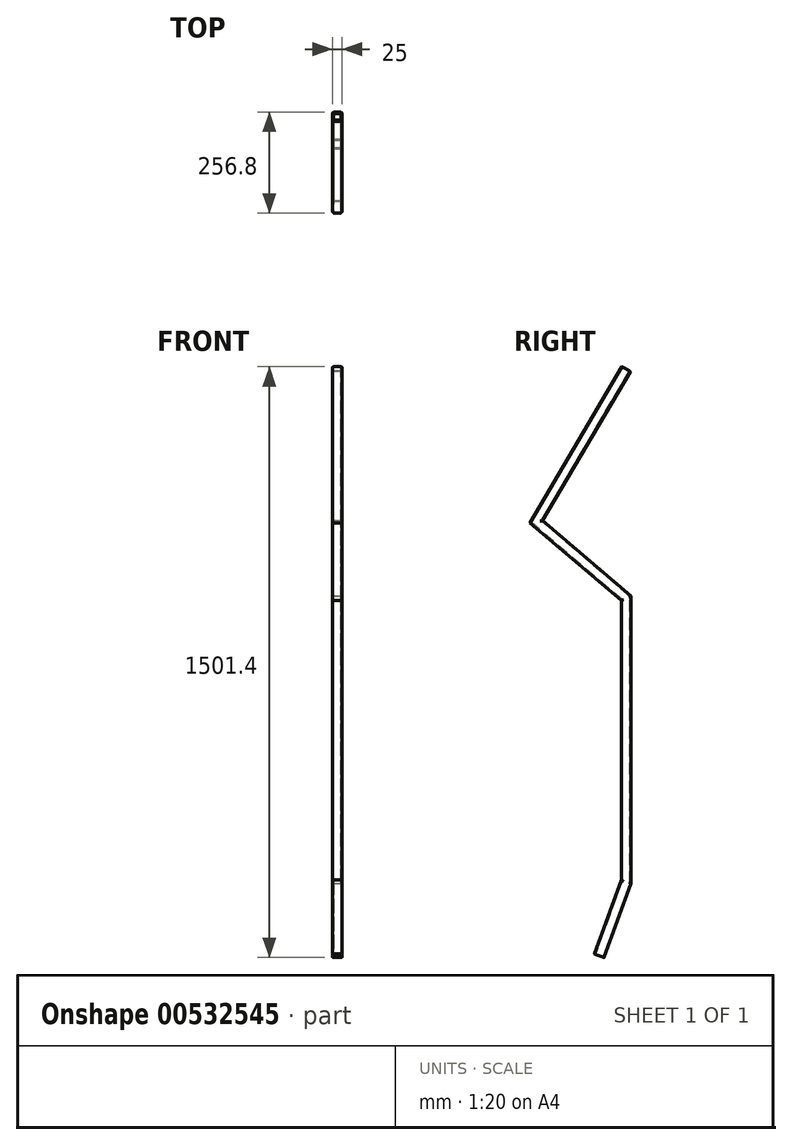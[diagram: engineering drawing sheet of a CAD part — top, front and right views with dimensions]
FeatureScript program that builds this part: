
annotation { "Feature Type Name" : "Feature", "Feature Type Description" : "" }
export const myFeature = defineFeature(function(context is Context, id is Id, definition is map)
    precondition{}
    {
        {
            var Q0;
            Q0=qCreatedBy(makeId("Right.planeOp"),FACE);
            var sketch = newSketch(context, id + "F0", { "sketchPlane" : qUnion([Q0])});
            skLineSegment(sketch, "E0", {"start": v(0, 1302.57) * mm, "end": v(-228.21, 914.73) * mm});
            skLineSegment(sketch, "E1", {"start": v(-228.21, 914.73) * mm, "end": v(0, 720) * mm});
            skLineSegment(sketch, "E2", {"start": v(0, 720) * mm, "end": v(0, 0) * mm});
            skSolve(sketch);
        }
        {
            var Q0;
            Q0=qCreatedBy(makeId("Top.planeOp"),FACE);
            var sketch = newSketch(context, id + "F1", { "sketchPlane" : qUnion([Q0])});
            skLineSegment(sketch, "E3.bottom", {"start": v(7.5, 12.5) * mm, "end": v(-7.5, 12.5) * mm});
            skLineSegment(sketch, "E3.top", {"start": v(7.5, -12.5) * mm, "end": v(-7.5, -12.5) * mm});
            skLineSegment(sketch, "E3.left", {"start": v(12.5, 7.5) * mm, "end": v(12.5, -7.5) * mm});
            skLineSegment(sketch, "E3.right", {"start": v(-12.5, 7.5) * mm, "end": v(-12.5, -7.5) * mm});
            skPoint(sketch, "E3.middle", {"position": v(0, 0) * mm});
            skPoint(sketch, "E4.visualSharp", {"position": v(-12.5, 12.5) * mm});
            skArc(sketch, "E4.filletArc", {"start": v(-7.5, 12.5) * mm, "mid": v(-11.04, 11.04) * mm, "end": v(-12.5, 7.5) * mm});
            skPoint(sketch, "E5.visualSharp", {"position": v(12.5, 12.5) * mm});
            skArc(sketch, "E5.filletArc", {"start": v(12.5, 7.5) * mm, "mid": v(11.04, 11.04) * mm, "end": v(7.5, 12.5) * mm});
            skPoint(sketch, "E6.visualSharp", {"position": v(12.5, -12.5) * mm});
            skArc(sketch, "E6.filletArc", {"start": v(7.5, -12.5) * mm, "mid": v(11.04, -11.04) * mm, "end": v(12.5, -7.5) * mm});
            skPoint(sketch, "E7.visualSharp", {"position": v(-12.5, -12.5) * mm});
            skArc(sketch, "E7.filletArc", {"start": v(-12.5, -7.5) * mm, "mid": v(-11.04, -11.04) * mm, "end": v(-7.5, -12.5) * mm});
            skArc(sketch, "E8.0", {"start": v(10, 7.5) * mm, "mid": v(9.27, 9.27) * mm, "end": v(7.5, 10) * mm});
            skLineSegment(sketch, "E8.1", {"start": v(10, 7.5) * mm, "end": v(10, -7.5) * mm});
            skLineSegment(sketch, "E8.2", {"start": v(7.5, 10) * mm, "end": v(-7.5, 10) * mm});
            skArc(sketch, "E8.3", {"start": v(7.5, -10) * mm, "mid": v(9.27, -9.27) * mm, "end": v(10, -7.5) * mm});
            skArc(sketch, "E8.4", {"start": v(-7.5, 10) * mm, "mid": v(-9.27, 9.27) * mm, "end": v(-10, 7.5) * mm});
            skLineSegment(sketch, "E8.5", {"start": v(-10, 7.5) * mm, "end": v(-10, -7.5) * mm});
            skArc(sketch, "E8.6", {"start": v(-10, -7.5) * mm, "mid": v(-9.27, -9.27) * mm, "end": v(-7.5, -10) * mm});
            skLineSegment(sketch, "E8.7", {"start": v(7.5, -10) * mm, "end": v(-7.5, -10) * mm});
            skSolve(sketch);
        }
        {
            var Q0;
            Q0 = qSketchRegion(id + "F1", true);
            var Q1;
            Q1 = qConstructionFilter(qBodyType(qCreatedBy(id + "F0" ,EDGE), BodyType.WIRE), ConstructionObject.NO);
            sweep(context, id + "F2", {"profiles" : qUnion([Q0]), "path" : qUnion([Q1])});
        }
        {
            var Q0;
            Q0=qCreatedBy(makeId("Right.planeOp"),FACE);
            var sketch = newSketch(context, id + "F3", { "sketchPlane" : qUnion([Q0])});
            skLineSegment(sketch, "E9", {"start": v(0, 0) * mm, "end": v(-68.4, -187.94) * mm});
            skSolve(sketch);
        }
        {
            var Q0;
            Q0=makeQuery(id+"F2.opSweep","SWEPT_FACE",FACE,{"disambiguationData":[OSD([sQuery(id+"F0.wireOp",EDGE,"E2"),sQuery(id+"F1.wireOp",EDGE,"E3.left")])]});
            var sketch = newSketch(context, id + "F4", { "sketchPlane" : qUnion([Q0])});
            skLineSegment(sketch, "E10", {"start": v(0, 0) * mm, "end": v(-12.5, 4.55) * mm});
            skLineSegment(sketch, "E11", {"start": v(-12.5, 4.55) * mm, "end": v(-12.5, 0) * mm});
            skLineSegment(sketch, "E12", {"start": v(-12.5, 0) * mm, "end": v(0, 0) * mm});
            skSolve(sketch);
        }
        {
            var Q0;
            Q0 = qSketchRegion(id + "F4", true);
            extrude(context, id + "F5", {"entities" : qUnion([Q0]), "operationType" : NewBodyOperationType.REMOVE, "endBound" : BoundingType.THROUGH_ALL, "oppositeDirection" : true, "depth" : 25 * mm, "offsetDistance" : 25 * mm});
        }
        {
            var Q0;
            Q0=makeQuery(id+"F2.opSweep","CAP_FACE",FACE,{"disambiguationData":[OSD([sQuery(id+"F0.wireOp",VERTEX,"E2.end"),sQuery(id+"F1.wireOp",EDGE,"E3.bottom"),sQuery(id+"F1.wireOp",EDGE,"E3.top"),sQuery(id+"F1.wireOp",EDGE,"E3.left"),sQuery(id+"F1.wireOp",EDGE,"E3.right"),sQuery(id+"F1.wireOp",EDGE,"E4.filletArc"),sQuery(id+"F1.wireOp",EDGE,"E5.filletArc"),sQuery(id+"F1.wireOp",EDGE,"E6.filletArc"),sQuery(id+"F1.wireOp",EDGE,"E7.filletArc"),sQuery(id+"F1.wireOp",EDGE,"E8.0"),sQuery(id+"F1.wireOp",EDGE,"E8.1"),sQuery(id+"F1.wireOp",EDGE,"E8.2"),sQuery(id+"F1.wireOp",EDGE,"E8.3"),sQuery(id+"F1.wireOp",EDGE,"E8.4"),sQuery(id+"F1.wireOp",EDGE,"E8.5"),sQuery(id+"F1.wireOp",EDGE,"E8.6"),sQuery(id+"F1.wireOp",EDGE,"E8.7")])],"isStart":true});
            var Q1;
            Q1=makeQuery(id+"F5.boolean.opBoolean","COPY",FACE,{"derivedFrom":makeQuery(id+"F5.opExtrude","SWEPT_FACE",FACE,{"disambiguationData":[OSD([sQuery(id+"F4.wireOp",EDGE,"E10")])]})});
            extrude(context, id + "F6", {"entities" : qUnion([Q0]), "operationType" : NewBodyOperationType.ADD, "endBound" : BoundingType.UP_TO_SURFACE, "depth" : 25 * mm, "endBoundEntityFace" : qUnion([Q1]), "offsetDistance" : 25 * mm});
        }
        {
            var Q0;
            {var subQ0=sQuery(id+"F4.wireOp",EDGE,"E10");Q0=makeQuery(id+"F6.boolean.opBoolean","MERGE",FACE,{"derivedFrom":[makeQuery(id+"F5.boolean.opBoolean","COPY",FACE,{"derivedFrom":makeQuery(id+"F5.opExtrude","SWEPT_FACE",FACE,{"disambiguationData":[OSD([subQ0])]})}),makeQuery(id+"F6.opExtrude","CAP_FACE",FACE,{"disambiguationData":[OSD([subQ0])],"isStart":false})]});}
            var Q1;
            Q1=sQuery(id+"F3.wireOp",EDGE,"E9");
            sweep(context, id + "F7", {"operationType" : NewBodyOperationType.ADD, "profiles" : qUnion([Q0]), "path" : qUnion([Q1])});
        }
    });
